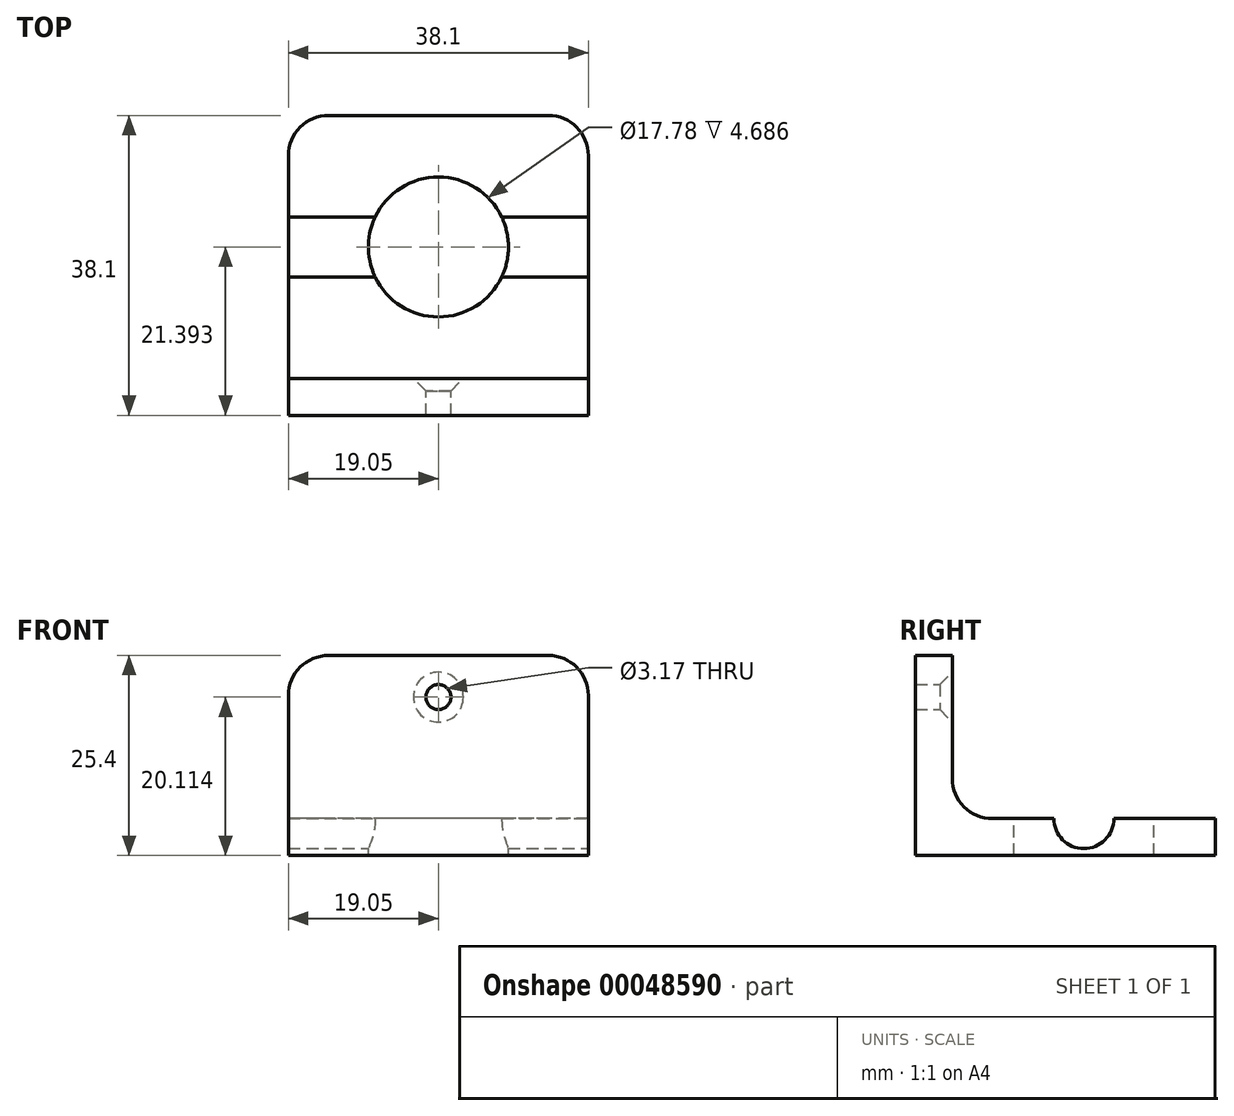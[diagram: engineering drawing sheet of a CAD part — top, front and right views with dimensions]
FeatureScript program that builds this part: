
annotation { "Feature Type Name" : "Feature", "Feature Type Description" : "" }
export const myFeature = defineFeature(function(context is Context, id is Id, definition is map)
    precondition{}
    {
        {
            var Q0;
            Q0=qCreatedBy(makeId("Right.planeOp"),FACE);
            var sketch = newSketch(context, id + "F0", { "sketchPlane" : qUnion([Q0])});
            skLineSegment(sketch, "E0", {"start": v(0, 25.4) * mm, "end": v(0, 0) * mm});
            skLineSegment(sketch, "E1", {"start": v(0, 0) * mm, "end": v(38.1, 0) * mm});
            skLineSegment(sketch, "E2.0", {"start": v(4.69, 4.69) * mm, "end": v(38.1, 4.69) * mm});
            skLineSegment(sketch, "E2.1", {"start": v(4.69, 25.4) * mm, "end": v(4.69, 4.69) * mm});
            skLineSegment(sketch, "E3", {"start": v(0, 25.4) * mm, "end": v(4.69, 25.4) * mm});
            skLineSegment(sketch, "E4", {"start": v(38.1, 4.69) * mm, "end": v(38.1, 0) * mm});
            skSolve(sketch);
        }
        {
            var Q0;
            Q0=makeQuery(id+"F0.imprint","IMPRINT",FACE,{"disambiguationData":[TD([[makeQuery(id+"F0.imprint","IMPRINT",EDGE,{"derivedFrom":sQuery(id+"F0.wireOp",EDGE,"E0")}),1.0]])]});
            extrude(context, id + "F1", {"entities" : qUnion([Q0]), "endBound" : BoundingType.SYMMETRIC, "depth" : 38.1 * mm});
        }
        {
            var Q0;
            Q0=makeQuery(id+"F1.opExtrude","SWEPT_FACE",FACE,{"disambiguationData":[OSD([sQuery(id+"F0.wireOp",EDGE,"E2.1")])]});
            var sketch = newSketch(context, id + "F2", { "sketchPlane" : qUnion([Q0])});
            skPoint(sketch, "E5", {"position": v(0, 20.11) * mm});
            skSolve(sketch);
        }
        {
            var Q0;
            Q0=sQuery(id+"F2.wireOp",VERTEX,"E5");
            var Q1;
            Q1=makeQuery(id+"F1.opExtrude","SWEPT_BODY",BODY,{"disambiguationData":[OSD([sQuery(id+"F0.wireOp",EDGE,"E0"),sQuery(id+"F0.wireOp",EDGE,"E1"),sQuery(id+"F0.wireOp",EDGE,"E2.0"),sQuery(id+"F0.wireOp",EDGE,"E2.1"),sQuery(id+"F0.wireOp",EDGE,"E3"),sQuery(id+"F0.wireOp",EDGE,"E4")])]});
            hole(context, id + "F3", {"style" : HoleStyle.C_SINK, "holeDiameter" : 3.17 * mm, "cSinkDiameter" : 6.35 * mm, "endStyle" : HoleEndStyle.THROUGH, "locations" : qUnion([Q0]), "scope" : qUnion([Q1]), "cSinkAngle" : 90 * degree});
        }
        {
            var Q0;
            Q0=makeQuery(id+"F1.opExtrude","SWEPT_FACE",FACE,{"disambiguationData":[OSD([sQuery(id+"F0.wireOp",EDGE,"E2.0")])]});
            var sketch = newSketch(context, id + "F4", { "sketchPlane" : qUnion([Q0])});
            skPoint(sketch, "E6", {"position": v(0, 21.4) * mm});
            skLineSegment(sketch, "E7", {"start": v(0, 38.1) * mm, "end": v(0, 4.69) * mm, "construction": true});
            skSolve(sketch);
        }
        {
            var Q0;
            Q0=sQuery(id+"F4.wireOp",VERTEX,"E6");
            var Q1;
            Q1=makeQuery(id+"F1.opExtrude","SWEPT_BODY",BODY,{"disambiguationData":[OSD([sQuery(id+"F0.wireOp",EDGE,"E0"),sQuery(id+"F0.wireOp",EDGE,"E1"),sQuery(id+"F0.wireOp",EDGE,"E2.0"),sQuery(id+"F0.wireOp",EDGE,"E2.1"),sQuery(id+"F0.wireOp",EDGE,"E3"),sQuery(id+"F0.wireOp",EDGE,"E4")])]});
            hole(context, id + "F5", {"style" : HoleStyle.SIMPLE, "holeDiameter" : 17.78 * mm, "endStyle" : HoleEndStyle.THROUGH, "locations" : qUnion([Q0]), "scope" : qUnion([Q1])});
        }
        {
            var Q0;
            Q0=makeQuery(id+"F1.opExtrude","CAP_FACE",FACE,{"disambiguationData":[OSD([sQuery(id+"F0.wireOp",EDGE,"E0"),sQuery(id+"F0.wireOp",EDGE,"E1"),sQuery(id+"F0.wireOp",EDGE,"E2.0"),sQuery(id+"F0.wireOp",EDGE,"E2.1"),sQuery(id+"F0.wireOp",EDGE,"E3"),sQuery(id+"F0.wireOp",EDGE,"E4")])],"isStart":false});
            var sketch = newSketch(context, id + "F6", { "sketchPlane" : qUnion([Q0])});
            skArc(sketch, "E8", {"start": v(17.58, 4.69) * mm, "mid": v(21.4, 0.88) * mm, "end": v(25.2, 4.69) * mm});
            skSolve(sketch);
        }
        {
            var Q0;
            {var subQ1=sQuery(id+"F6.wireOp",EDGE,"E8");Q0=makeQuery(id+"F6.imprint","IMPRINT",FACE,{"disambiguationData":[TD([[makeQuery(id+"F6.imprint","IMPRINT",EDGE,{"derivedFrom":subQ1}),1.0]])]});}
            extrude(context, id + "F7", {"entities" : qUnion([Q0]), "operationType" : NewBodyOperationType.REMOVE, "endBound" : BoundingType.THROUGH_ALL, "oppositeDirection" : true, "depth" : 25.4 * mm});
        }
        {
            var Q0;
            Q0=makeQuery(id+"F1.opExtrude","SWEPT_EDGE",EDGE,{"disambiguationData":[OSD([sQuery(id+"F0.wireOp",EDGE,"E2.0"),sQuery(id+"F0.wireOp",EDGE,"E2.1")])]});
            fillet(context, id + "F8", {"entities" : qUnion([Q0]), "radius" : 5.08 * mm, "tangentPropagation" : true, "allowEdgeOverflow" : false});
        }
        {
            var Q0;
            Q0=makeQuery(id+"F1.opExtrude","CAP_EDGE",EDGE,{"disambiguationData":[OSD([sQuery(id+"F0.wireOp",EDGE,"E4")])],"isStart":false});
            var Q1;
            Q1=makeQuery(id+"F1.opExtrude","CAP_EDGE",EDGE,{"disambiguationData":[OSD([sQuery(id+"F0.wireOp",EDGE,"E4")])],"isStart":true});
            var Q2;
            Q2=makeQuery(id+"F1.opExtrude","CAP_EDGE",EDGE,{"disambiguationData":[OSD([sQuery(id+"F0.wireOp",EDGE,"E3")])],"isStart":false});
            var Q3;
            Q3=makeQuery(id+"F1.opExtrude","CAP_EDGE",EDGE,{"disambiguationData":[OSD([sQuery(id+"F0.wireOp",EDGE,"E3")])],"isStart":true});
            fillet(context, id + "F9", {"entities" : qUnion([Q0, Q1, Q2, Q3]), "radius" : 5.08 * mm, "tangentPropagation" : true, "allowEdgeOverflow" : false});
        }
    });
